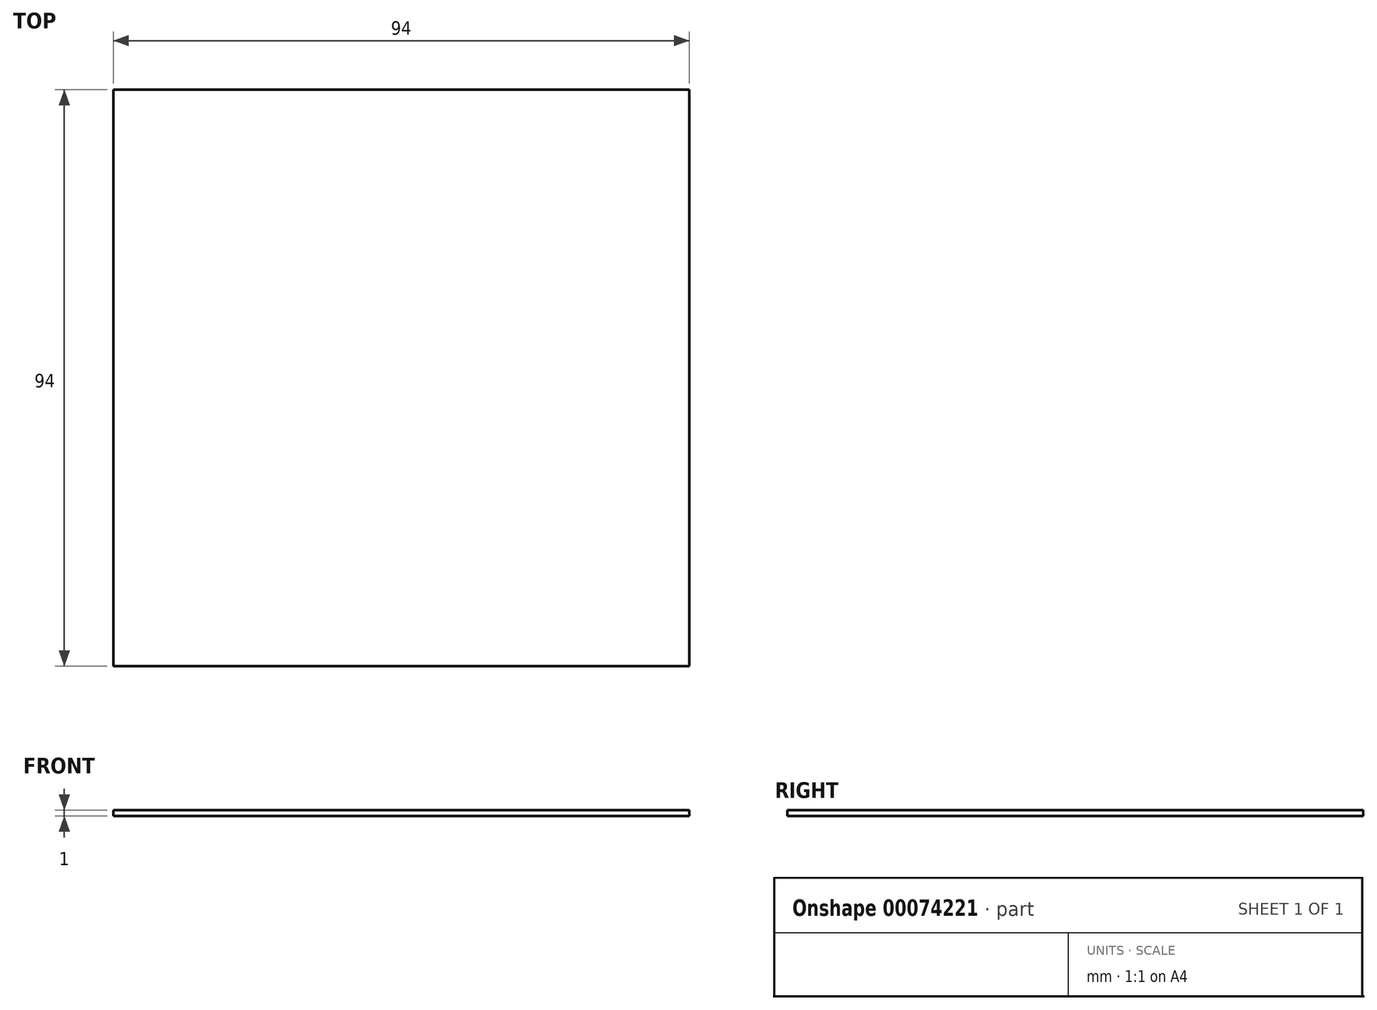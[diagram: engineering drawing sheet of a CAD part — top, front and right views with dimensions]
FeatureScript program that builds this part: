
annotation { "Feature Type Name" : "Feature", "Feature Type Description" : "" }
export const myFeature = defineFeature(function(context is Context, id is Id, definition is map)
    precondition{}
    {
        {
            var Q0;
            Q0=qCreatedBy(makeId("Top.planeOp"),FACE);
            var sketch = newSketch(context, id + "F0", { "sketchPlane" : qUnion([Q0])});
            skLineSegment(sketch, "E0.bottom", {"start": v(-47, 47) * mm, "end": v(47, 47) * mm});
            skLineSegment(sketch, "E0.top", {"start": v(-47, -47) * mm, "end": v(47, -47) * mm});
            skLineSegment(sketch, "E0.left", {"start": v(-47, 47) * mm, "end": v(-47, -47) * mm});
            skLineSegment(sketch, "E0.right", {"start": v(47, 47) * mm, "end": v(47, -47) * mm});
            skLineSegment(sketch, "E1", {"start": v(-47, 0) * mm, "end": v(47, 0) * mm, "construction": true});
            skLineSegment(sketch, "E2", {"start": v(0, 47) * mm, "end": v(0, -47) * mm, "construction": true});
            skSolve(sketch);
        }
        {
            var Q0;
            Q0=qSketchRegion(id+"F0",true);
            extrude(context, id + "F1", {"entities" : qUnion([Q0]), "oppositeDirection" : true, "depth" : 1 * mm});
        }
    });
